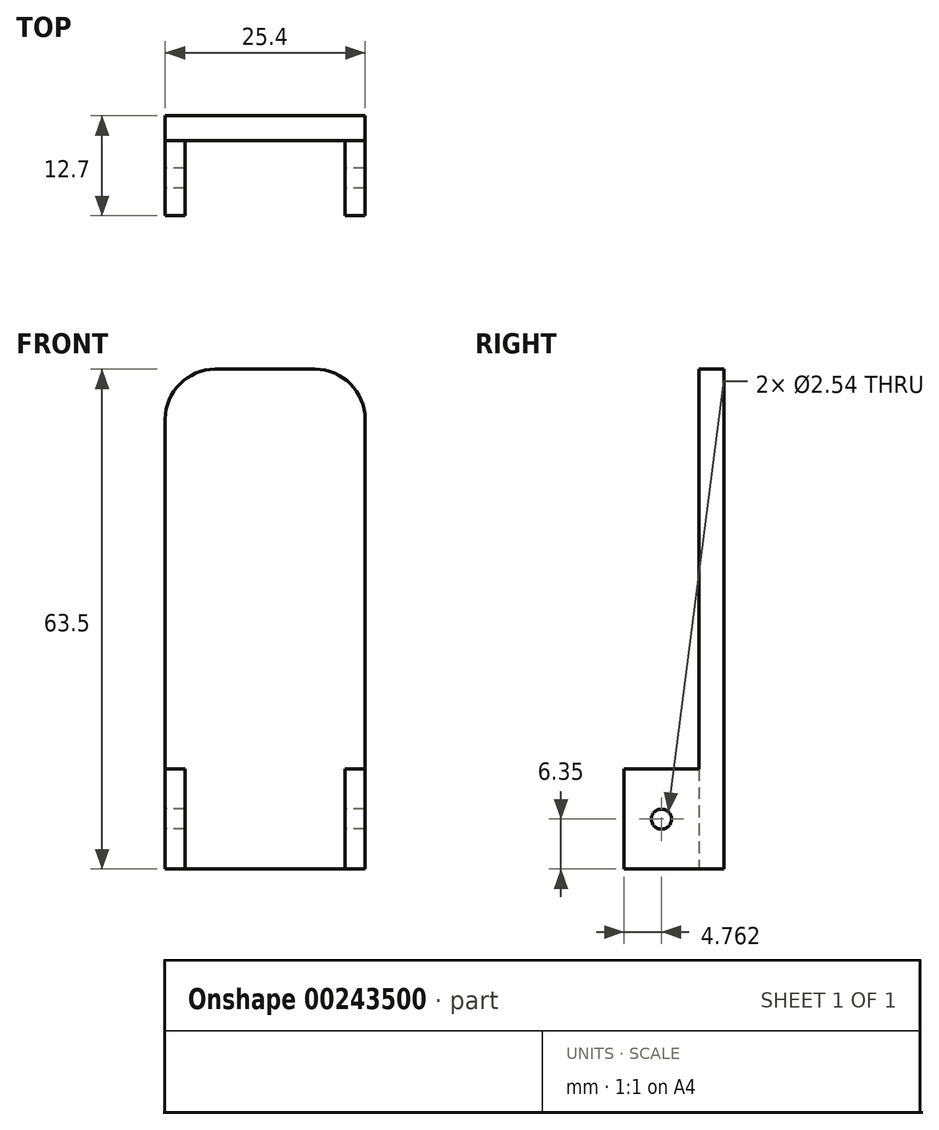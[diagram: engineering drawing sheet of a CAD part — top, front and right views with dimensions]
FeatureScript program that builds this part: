
annotation { "Feature Type Name" : "Feature", "Feature Type Description" : "" }
export const myFeature = defineFeature(function(context is Context, id is Id, definition is map)
    precondition{}
    {
        {
            var Q0;
            Q0=qCreatedBy(makeId("Front.planeOp"),FACE);
            var sketch = newSketch(context, id + "F0", { "sketchPlane" : qUnion([Q0])});
            skLineSegment(sketch, "E0.bottom", {"start": v(12.7, -31.75) * mm, "end": v(-12.7, -31.75) * mm});
            skLineSegment(sketch, "E0.top", {"start": v(6.35, 31.75) * mm, "end": v(-6.35, 31.75) * mm});
            skLineSegment(sketch, "E0.left", {"start": v(12.7, -31.75) * mm, "end": v(12.7, 25.4) * mm});
            skLineSegment(sketch, "E0.right", {"start": v(-12.7, -31.75) * mm, "end": v(-12.7, 25.4) * mm});
            skPoint(sketch, "E0.middle", {"position": v(0, 0) * mm});
            skPoint(sketch, "E1.visualSharp", {"position": v(-12.7, 31.75) * mm});
            skArc(sketch, "E1.filletArc", {"start": v(-6.35, 31.75) * mm, "mid": v(-10.84, 29.9) * mm, "end": v(-12.7, 25.4) * mm});
            skPoint(sketch, "E2.visualSharp", {"position": v(12.7, 31.75) * mm});
            skArc(sketch, "E2.filletArc", {"start": v(12.7, 25.4) * mm, "mid": v(10.84, 29.9) * mm, "end": v(6.35, 31.75) * mm});
            skSolve(sketch);
        }
        {
            var Q0;
            Q0=makeQuery(id+"F0.imprint","IMPRINT",FACE,{"disambiguationData":[TD([[makeQuery(id+"F0.imprint","IMPRINT",EDGE,{"derivedFrom":sQuery(id+"F0.wireOp",EDGE,"E0.bottom")}),-1.0]])]});
            extrude(context, id + "F1", {"entities" : qUnion([Q0]), "depth" : 3.17 * mm});
        }
        {
            var Q0;
            Q0=qCreatedBy(makeId("Front.planeOp"),FACE);
            var sketch = newSketch(context, id + "F2", { "sketchPlane" : qUnion([Q0])});
            skPoint(sketch, "E3.0", {"position": v(12.7, -31.75) * mm});
            skPoint(sketch, "E4.0", {"position": v(-12.7, -31.75) * mm});
            skLineSegment(sketch, "E5.bottom", {"start": v(12.7, -31.75) * mm, "end": v(-12.7, -31.75) * mm});
            skLineSegment(sketch, "E5.top", {"start": v(12.7, -19.05) * mm, "end": v(-12.7, -19.05) * mm});
            skLineSegment(sketch, "E5.left", {"start": v(12.7, -31.75) * mm, "end": v(12.7, -19.05) * mm});
            skLineSegment(sketch, "E5.right", {"start": v(-12.7, -31.75) * mm, "end": v(-12.7, -19.05) * mm});
            skLineSegment(sketch, "E6.bottom", {"start": v(0, -31.75) * mm, "end": v(10.16, -31.75) * mm});
            skLineSegment(sketch, "E6.top", {"start": v(0, -19.05) * mm, "end": v(10.16, -19.05) * mm});
            skLineSegment(sketch, "E6.left", {"start": v(0, -31.75) * mm, "end": v(0, -19.05) * mm});
            skLineSegment(sketch, "E6.right", {"start": v(10.16, -31.75) * mm, "end": v(10.16, -19.05) * mm});
            skLineSegment(sketch, "E7.bottom", {"start": v(0, -31.75) * mm, "end": v(-10.16, -31.75) * mm});
            skLineSegment(sketch, "E7.top", {"start": v(0, -19.05) * mm, "end": v(-10.16, -19.05) * mm});
            skLineSegment(sketch, "E7.right", {"start": v(-10.16, -31.75) * mm, "end": v(-10.16, -19.05) * mm});
            skSolve(sketch);
        }
        {
            var Q0;
            {var subQ0=sQuery(id+"F2.wireOp",EDGE,"E5.left");Q0=makeQuery(id+"F2.imprint","IMPRINT",FACE,{"disambiguationData":[TD([[makeQuery(id+"F2.imprint","IMPRINT",EDGE,{"derivedFrom":subQ0}),1.0]])]});}
            var Q1;
            {var subQ0=sQuery(id+"F2.wireOp",EDGE,"E5.right");Q1=makeQuery(id+"F2.imprint","IMPRINT",FACE,{"disambiguationData":[TD([[makeQuery(id+"F2.imprint","IMPRINT",EDGE,{"derivedFrom":subQ0}),-1.0]])]});}
            extrude(context, id + "F3", {"entities" : qUnion([Q0, Q1]), "operationType" : NewBodyOperationType.ADD, "depth" : 12.7 * mm});
        }
        {
            var Q0;
            Q0=makeQuery(id+"F3.boolean.opBoolean","MERGE",FACE,{"derivedFrom":[makeQuery(id+"F1.opExtrude","SWEPT_FACE",FACE,{"disambiguationData":[OSD([sQuery(id+"F0.wireOp",EDGE,"E0.left")])]}),makeQuery(id+"F3.opExtrude","SWEPT_FACE",FACE,{"disambiguationData":[OSD([sQuery(id+"F2.wireOp",EDGE,"E5.left")])]})]});
            var sketch = newSketch(context, id + "F4", { "sketchPlane" : qUnion([Q0])});
            skPoint(sketch, "E8", {"position": v(-7.94, -25.4) * mm});
            skPoint(sketch, "E8.positionSnap0", {"position": v(-12.7, -25.4) * mm});
            skPoint(sketch, "E8.positionSnap1", {"position": v(-7.94, -19.05) * mm});
            skSolve(sketch);
        }
        {
            var Q0;
            Q0=sQuery(id+"F4.wireOp",VERTEX,"E8");
            var Q1;
            Q1=makeQuery(id+"F1.opExtrude","SWEPT_BODY",BODY,{"disambiguationData":[OSD([sQuery(id+"F0.wireOp",EDGE,"E0.bottom"),sQuery(id+"F0.wireOp",EDGE,"E0.top"),sQuery(id+"F0.wireOp",EDGE,"E0.left"),sQuery(id+"F0.wireOp",EDGE,"E0.right"),sQuery(id+"F0.wireOp",EDGE,"E1.filletArc"),sQuery(id+"F0.wireOp",EDGE,"E2.filletArc")])]});
            hole(context, id + "F5", {"style" : HoleStyle.SIMPLE, "endStyle" : HoleEndStyle.THROUGH, "holeDiameter" : 2.54 * mm, "tappedDepth" : 12.7 * mm, "tapClearance" : 3, "locations" : qUnion([Q0]), "scope" : qUnion([Q1]), "startStyle" : HoleStartStyle.PART});
        }
    });
